# Revit family: 8100E FAAST aspirasjonsdetektor
name_source: partatom
category: Fire Alarm Devices
revit_build: Autodesk Revit 2016 (Build: 20160314_0715(x64)
units: mm (PartAtom-declared; Revit-internal decimal feet)

## family parameters
Always vertical = Yes
Cut with Voids When Loaded = No
Maintain Annotation Orientation = No
OmniClass Number = 23.85.30.21
OmniClass Title = Environmental Detection/Registration
Part Type = Normal
Room Calculation Point = No
Round Connector Dimension = Use Diameter
Shared = No
Work Plane-Based = No

## types (1)
- RY5422
    Assembly Code = 5423
    CQ Voltage = 230 V
    Keynote = XN3
    Load = 0 VA
    Manufacturer = Honeywell
    Material = Plastic - Dark Grey
    NS8360 = 5423_XN3
    NVType = ASP
    NVTypeTekstSynlig = Yes
    b = 330 mm
    d = 127 mm
    h = 337 mm  [stored 1.10564 ft]

note: [stored X ft] marks values corroborated as IEEE doubles in the binary element streams (Revit-internal decimal feet)

## geometry (parser evidence)
native form markers: Sweep x4
no freeform markers — native parametric forms only
